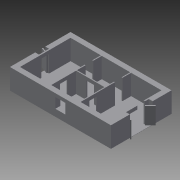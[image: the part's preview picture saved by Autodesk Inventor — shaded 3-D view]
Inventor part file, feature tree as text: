
AUTODESK INVENTOR PART (.ipt)
format: ipt  version: 2013 SP2 (Build 170200200, 200)  size: 379,392 bytes
history: native  units: in
note: dims shown in document units (in); Inventor stores cm internally (conversion verified against a paired STEP export)
features: extrude x9, sketch x8, projected_geometry x6, other x1
ambient origin geometry x8: Origin, YZ Plane, XZ Plane, XY Plane, X Axis, Y Axis, Z Axis, Center Point
bodies: Solid1 (feature_tree)
feature tree (24):
  extrude  "Extrusion1"  Depth=24.0in
  extrude  "Extrusion2"  Depth=4.5in
  extrude  "Extrusion3"  Depth=168.0in
  extrude  "Extrusion5"  Depth=36.0in
  extrude  "Extrusion6"  Depth=4.5in
  extrude  "Extrusion7"  Depth=40.875in
  extrude  "Extrusion8"  Depth=36.0in
  extrude  "Extrusion9"  Depth=168.0in
  extrude  "Extrusion10"  Depth=72.0in
  sketch  "Sketch1"  dims[d0=480.0in d2=288.0in d3=24.0in d4=24.0in]
  sketch  "Sketch2"  dims[d6=4.5in d8=4.5in d9=4.5in]
  sketch  "Sketch3"  dims[d10=24.0in d12=168.0in]
  projected_geometry  "Projected Loop1"
  projected_geometry  "Projected Loop2"
  projected_geometry  "Projected Loop3"
  sketch  "Sketch5"  dims[d13=40.875in d14=36.0in]
  projected_geometry  "Projected Loop4"
  sketch  "Sketch6"  dims[d15=168.0in d16=4.5in d17=4.5in]
  projected_geometry  "Projected Loop5"
  sketch  "Sketch7"  dims[d18=40.875in d19=40.875in]
  sketch  "Sketch8"  dims[d20=36.0in d21=36.0in]
  sketch  "Sketch9"  dims[d22=480.0in d23=24.0in d24=168.0in d25=72.0in d26=480.0in d27=24.0in d28=4.5in d29=96.0in d30=0.0in d31=48.0in d33=48.0in d34=32.0in d35=96.0in d36=0.0in d37=16.0in d38=0.0in d43=1.0in d44=0.0in d46=6.0in d47=6.0in d48=1.0in d49=0.0in d50=1.0in d51=0.0in d52=18.0in d53=18.0in d54=6.0in d55=6.0in d56=1.0in d57=0.0in d58=1.0in d59=0.0in d60=36.0in d62=4.5in d63=36.0in d64=4.5in d65=36.0in d66=4.5in d67=80.0in d68=0.0in]
  projected_geometry  "Projected Loop6"
  other  "Open Doors"
